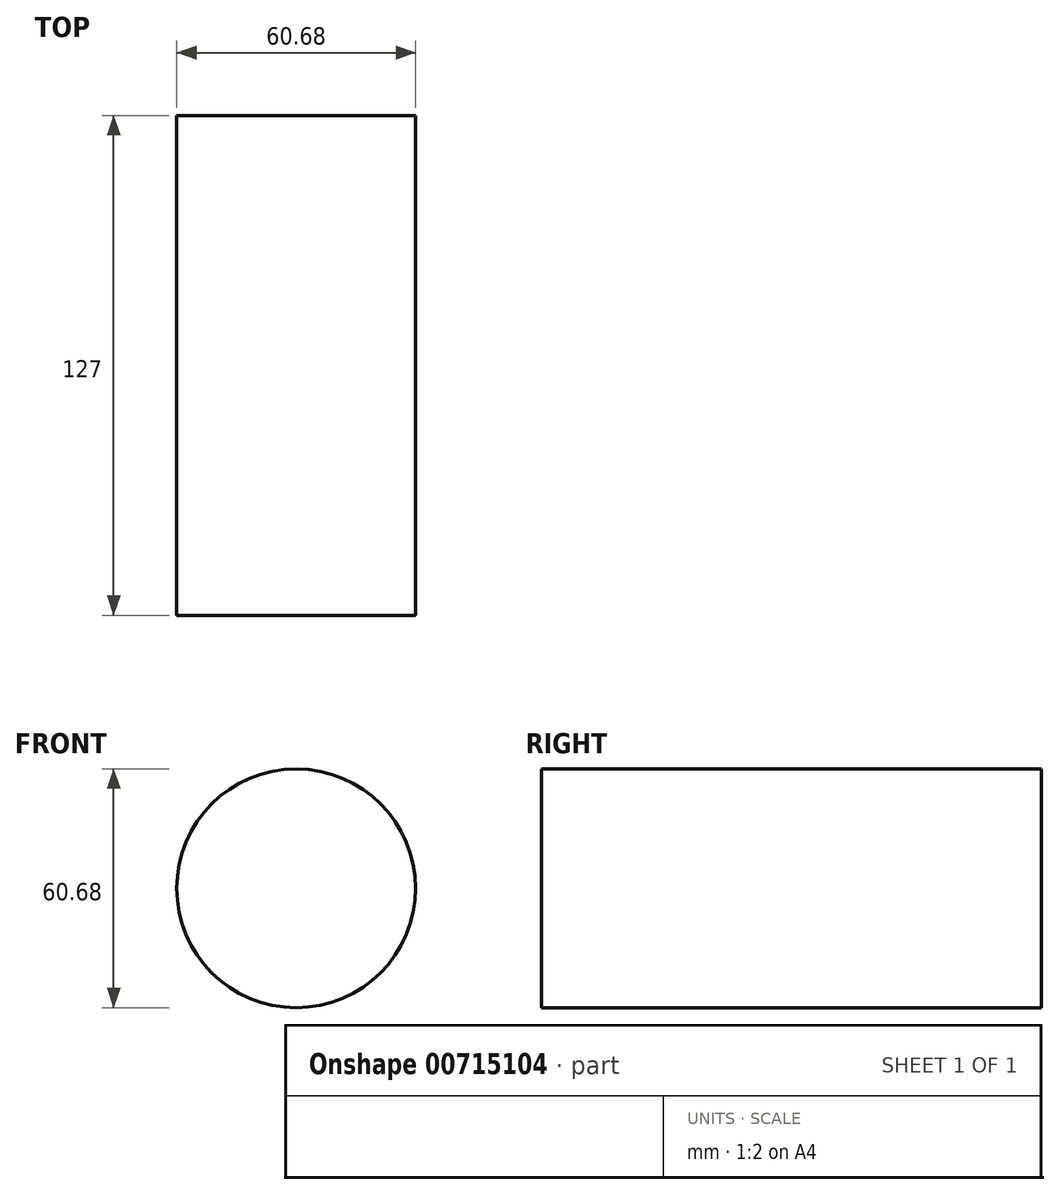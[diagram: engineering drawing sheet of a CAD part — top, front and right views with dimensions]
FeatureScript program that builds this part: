
annotation { "Feature Type Name" : "Feature", "Feature Type Description" : "" }
export const myFeature = defineFeature(function(context is Context, id is Id, definition is map)
    precondition{}
    {
        {
            var Q0;
            Q0=qCreatedBy(makeId("Front.planeOp"),FACE);
            var sketch = newSketch(context, id + "F0", { "sketchPlane" : qUnion([Q0])});
            skCircle(sketch, "E0", {"center": v(0, 0) * mm, "radius": 30.34 * mm});
            skSolve(sketch);
        }
        {
            var Q0;
            Q0=makeQuery(id+"F0.imprint","IMPRINT",FACE,{"disambiguationData":[TD([[makeQuery(id+"F0.imprint","IMPRINT",EDGE,{"derivedFrom":sQuery(id+"F0.wireOp",EDGE,"E0")}),1.0]])]});
            extrude(context, id + "F1", {"entities" : qUnion([Q0]), "depth" : 76.2 * mm, "offsetDistance" : 25.4 * mm, "hasSecondDirection" : true, "secondDirectionOppositeDirection" : true, "secondDirectionDepth" : 50.8 * mm});
        }
    });
